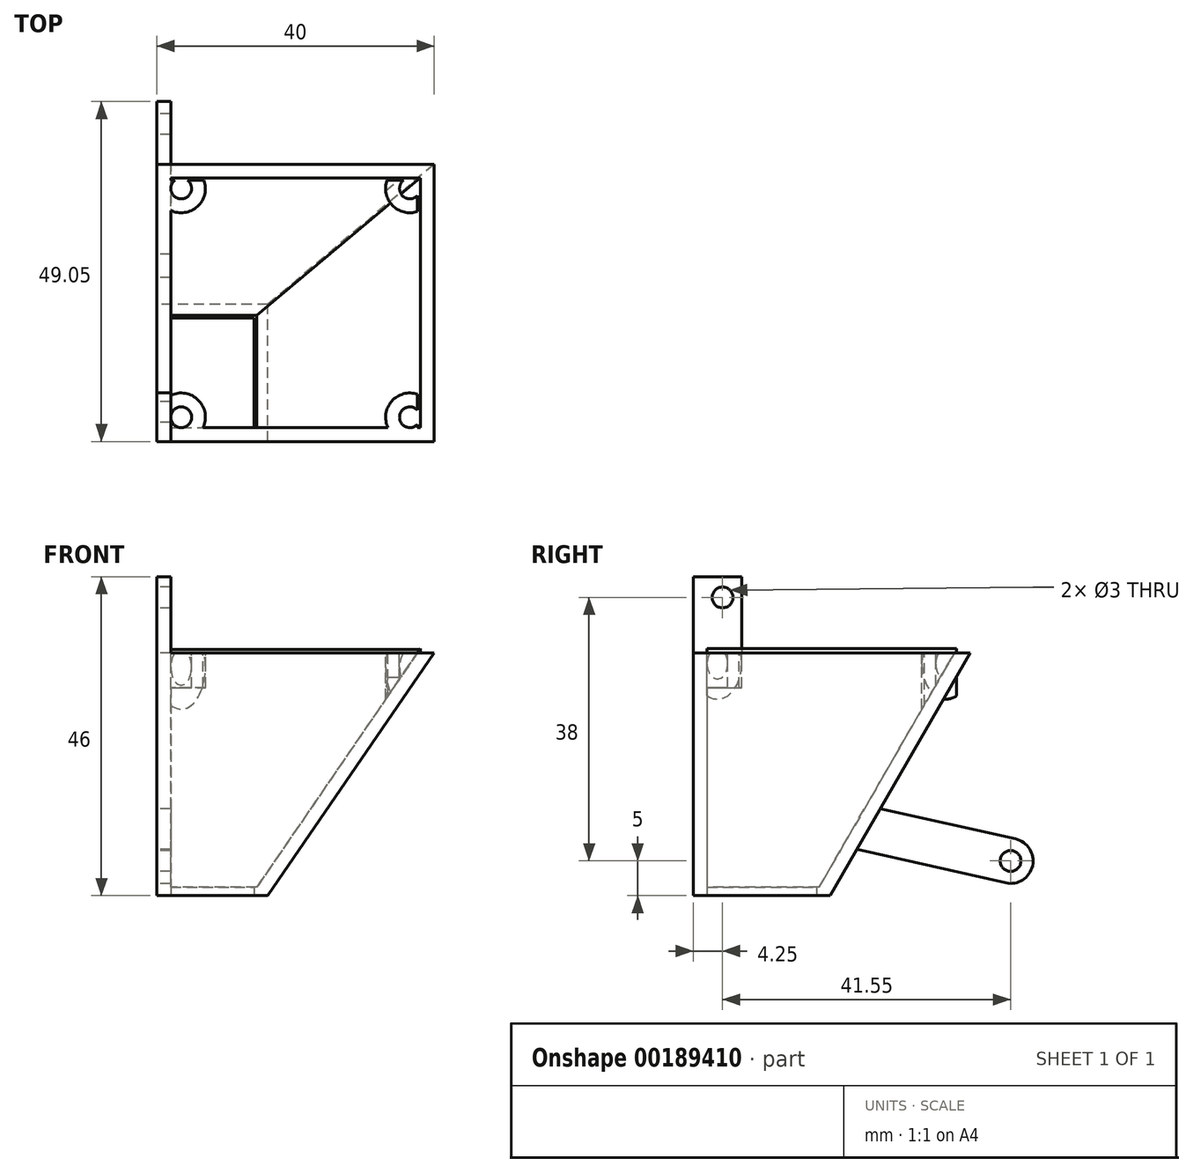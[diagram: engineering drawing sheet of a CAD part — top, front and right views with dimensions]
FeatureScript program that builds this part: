
annotation { "Feature Type Name" : "Feature", "Feature Type Description" : "" }
export const myFeature = defineFeature(function(context is Context, id is Id, definition is map)
    precondition{}
    {
        {
            var Q0;
            Q0=qCreatedBy(makeId("Top.planeOp"),FACE);
            var sketch = newSketch(context, id + "F0", { "sketchPlane" : qUnion([Q0])});
            skLineSegment(sketch, "E0.bottom", {"start": v(0, 0) * mm, "end": v(16, 0) * mm});
            skLineSegment(sketch, "E0.top", {"start": v(0, 19.8) * mm, "end": v(16, 19.8) * mm});
            skLineSegment(sketch, "E0.left", {"start": v(0, 0) * mm, "end": v(0, 19.8) * mm});
            skLineSegment(sketch, "E0.right", {"start": v(16, 0) * mm, "end": v(16, 19.8) * mm});
            skLineSegment(sketch, "E1.0", {"start": v(2, 17.8) * mm, "end": v(14, 17.8) * mm});
            skLineSegment(sketch, "E1.1", {"start": v(2, 2) * mm, "end": v(2, 17.8) * mm});
            skLineSegment(sketch, "E1.2", {"start": v(2, 2) * mm, "end": v(14, 2) * mm});
            skLineSegment(sketch, "E1.3", {"start": v(14, 2) * mm, "end": v(14, 17.8) * mm});
            skSolve(sketch);
        }
        {
            var Q0;
            Q0=qCreatedBy(makeId("Right.planeOp"),FACE);
            var sketch = newSketch(context, id + "F1", { "sketchPlane" : qUnion([Q0])});
            skLineSegment(sketch, "E2", {"start": v(0, 0) * mm, "end": v(0, 35) * mm});
            skLineSegment(sketch, "E3", {"start": v(0, 35) * mm, "end": v(19.8, 35) * mm});
            skLineSegment(sketch, "E4", {"start": v(19.8, 35) * mm, "end": v(40, 35) * mm});
            skLineSegment(sketch, "E5", {"start": v(40, 35) * mm, "end": v(19.8, 0) * mm});
            skLineSegment(sketch, "E6", {"start": v(0, 35) * mm, "end": v(0, 43) * mm, "construction": true});
            skLineSegment(sketch, "E7", {"start": v(0, 43) * mm, "end": v(4.25, 43) * mm, "construction": true});
            skCircle(sketch, "E8", {"center": v(4.25, 43) * mm, "radius": 1.5 * mm});
            skLineSegment(sketch, "E9", {"start": v(0, 35) * mm, "end": v(0, 46) * mm});
            skPoint(sketch, "E9.endSnap0", {"position": v(0, 39) * mm});
            skLineSegment(sketch, "E10", {"start": v(0, 46) * mm, "end": v(7, 46) * mm});
            skLineSegment(sketch, "E11", {"start": v(7, 46) * mm, "end": v(7, 35) * mm});
            skLineSegment(sketch, "E12", {"start": v(19.8, 0) * mm, "end": v(45.8, 0) * mm, "construction": true});
            skLineSegment(sketch, "E13", {"start": v(45.8, 0) * mm, "end": v(45.8, 5) * mm, "construction": true});
            skCircle(sketch, "E14", {"center": v(45.8, 5) * mm, "radius": 1.5 * mm});
            skCircle(sketch, "E15", {"center": v(45.8, 5) * mm, "radius": 3.25 * mm});
            skLineSegment(sketch, "E16", {"start": v(27.04, 12.55) * mm, "end": v(46.51, 8.17) * mm});
            skLineSegment(sketch, "E17", {"start": v(45.09, 1.83) * mm, "end": v(23.64, 6.65) * mm});
            skLineSegment(sketch, "E18", {"start": v(19.8, 0) * mm, "end": v(0, 0) * mm});
            skSolve(sketch);
        }
        {
            var Q0;
            Q0=qCreatedBy(makeId("Front.planeOp"),FACE);
            var sketch = newSketch(context, id + "F2", { "sketchPlane" : qUnion([Q0])});
            skLineSegment(sketch, "E19", {"start": v(40, 35) * mm, "end": v(16, 0) * mm});
            skLineSegment(sketch, "E20", {"start": v(40, 35) * mm, "end": v(0, 35) * mm});
            skLineSegment(sketch, "E21", {"start": v(0, 35) * mm, "end": v(0, 0) * mm});
            skLineSegment(sketch, "E22", {"start": v(0, 0) * mm, "end": v(16, 0) * mm});
            skSolve(sketch);
        }
        {
            var Q0;
            Q0=sQuery(id+"F2.wireOp",EDGE,"E19");
            var Q1;
            Q1=sQuery(id+"F0.wireOp",EDGE,"E0.right");
            cPlane(context, id + "F3", {"entities" : qUnion([Q0, Q1]), "cplaneType" : CPlaneType.LINE_ANGLE, "offset" : 25 * mm, "angle" : 0 * degree, "width" : 150 * mm, "height" : 150 * mm});
        }
        {
            var Q0;
            Q0=qCreatedBy(id+"F3.planeOp",FACE);
            var sketch = newSketch(context, id + "F4", { "sketchPlane" : qUnion([Q0])});
            skLineSegment(sketch, "E23", {"start": v(0, 51.49) * mm, "end": v(40, 51.49) * mm});
            skLineSegment(sketch, "E24", {"start": v(40, 51.49) * mm, "end": v(19.8, 9.05) * mm});
            skLineSegment(sketch, "E25", {"start": v(0, 51.49) * mm, "end": v(0, 9.05) * mm});
            skLineSegment(sketch, "E26", {"start": v(0, 9.05) * mm, "end": v(19.8, 9.05) * mm});
            skSolve(sketch);
        }
        {
            var Q0;
            Q0=sQuery(id+"F4.wireOp",EDGE,"E24");
            cPoint(context, id + "F5", {"entities" : qUnion([Q0]), "parameter" : 0.5});
        }
        {
            var Q0;
            Q0=sQuery(id+"F0.wireOp",EDGE,"E0.top");
            cPoint(context, id + "F6", {"entities" : qUnion([Q0]), "parameter" : 0.5});
        }
        {
            var Q0;
            Q0=sQuery(id+"F1.wireOp",EDGE,"E5");
            cPoint(context, id + "F7", {"entities" : qUnion([Q0]), "parameter" : 0.5});
        }
        {
            var Q0;
            Q0 = qCreatedBy(id + "F5" ,VERTEX);
            var Q1;
            Q1 = qCreatedBy(id + "F6" ,VERTEX);
            var Q2;
            Q2 = qCreatedBy(id + "F7" ,VERTEX);
            cPlane(context, id + "F8", {"entities" : qUnion([Q0, Q1, Q2]), "cplaneType" : CPlaneType.THREE_POINT, "offset" : 25 * mm, "width" : 150 * mm, "height" : 150 * mm});
        }
        {
            var Q0;
            Q0=qCreatedBy(id+"F8.planeOp",FACE);
            var sketch = newSketch(context, id + "F9", { "sketchPlane" : qUnion([Q0])});
            skLineSegment(sketch, "E27", {"start": v(40, 50.3) * mm, "end": v(0, 50.3) * mm});
            skLineSegment(sketch, "E28", {"start": v(40, 50.3) * mm, "end": v(16, 9.9) * mm});
            skLineSegment(sketch, "E29", {"start": v(16, 9.9) * mm, "end": v(0, 9.9) * mm});
            skLineSegment(sketch, "E30", {"start": v(0, 9.9) * mm, "end": v(0, 50.3) * mm});
            skSolve(sketch);
        }
        {
            var Q0;
            Q0=sQuery(id+"F4.wireOp",EDGE,"E23");
            cPoint(context, id + "F10", {"entities" : qUnion([Q0]), "parameter" : 0.5});
        }
        {
            var Q0;
            Q0=sQuery(id+"F2.wireOp",EDGE,"E20");
            cPoint(context, id + "F11", {"entities" : qUnion([Q0]), "parameter" : 0.5});
        }
        {
            var Q0;
            Q0=sQuery(id+"F1.wireOp",VERTEX,"E4.start");
            var Q1;
            Q1 = qCreatedBy(id + "F10" ,VERTEX);
            var Q2;
            Q2 = qCreatedBy(id + "F11" ,VERTEX);
            cPlane(context, id + "F12", {"entities" : qUnion([Q0, Q1, Q2]), "cplaneType" : CPlaneType.THREE_POINT, "offset" : 25 * mm, "width" : 150 * mm, "height" : 150 * mm});
        }
        {
            var Q0;
            Q0=qCreatedBy(id+"F12.planeOp",FACE);
            var sketch = newSketch(context, id + "F13", { "sketchPlane" : qUnion([Q0])});
            skLineSegment(sketch, "E31.bottom", {"start": v(0, 0) * mm, "end": v(40, 0) * mm});
            skLineSegment(sketch, "E31.top", {"start": v(0, 40) * mm, "end": v(40, 40) * mm});
            skLineSegment(sketch, "E31.left", {"start": v(0, 0) * mm, "end": v(0, 40) * mm});
            skLineSegment(sketch, "E31.right", {"start": v(40, 0) * mm, "end": v(40, 40) * mm});
            skLineSegment(sketch, "E32.0", {"start": v(2, 3.5) * mm, "end": v(2, 36.5) * mm});
            skLineSegment(sketch, "E32.1", {"start": v(3.5, 2) * mm, "end": v(36.5, 2) * mm});
            skLineSegment(sketch, "E32.2", {"start": v(38, 3.5) * mm, "end": v(38, 36.5) * mm});
            skLineSegment(sketch, "E32.3", {"start": v(3.5, 38) * mm, "end": v(36.5, 38) * mm});
            skCircle(sketch, "E33", {"center": v(3.5, 36.5) * mm, "radius": 1.5 * mm});
            skCircle(sketch, "E34", {"center": v(3.5, 3.5) * mm, "radius": 1.5 * mm});
            skCircle(sketch, "E35", {"center": v(36.5, 3.5) * mm, "radius": 1.5 * mm});
            skCircle(sketch, "E36", {"center": v(36.5, 36.5) * mm, "radius": 1.5 * mm});
            skArc(sketch, "E37", {"start": v(6.66, 2) * mm, "mid": v(5.97, 5.97) * mm, "end": v(2, 6.66) * mm});
            skArc(sketch, "E38", {"start": v(38, 6.66) * mm, "mid": v(34.03, 5.97) * mm, "end": v(33.34, 2) * mm});
            skArc(sketch, "E39", {"start": v(33.34, 38) * mm, "mid": v(34.03, 34.03) * mm, "end": v(38, 33.34) * mm});
            skArc(sketch, "E40", {"start": v(2, 33.34) * mm, "mid": v(5.97, 34.03) * mm, "end": v(6.66, 38) * mm});
            skLineSegment(sketch, "E41", {"start": v(2, 3.5) * mm, "end": v(2, 2) * mm});
            skLineSegment(sketch, "E42", {"start": v(2, 2) * mm, "end": v(3.5, 2) * mm});
            skLineSegment(sketch, "E43", {"start": v(2, 36.5) * mm, "end": v(2, 38) * mm});
            skLineSegment(sketch, "E44", {"start": v(2, 38) * mm, "end": v(3.5, 38) * mm});
            skLineSegment(sketch, "E45", {"start": v(36.5, 38) * mm, "end": v(38, 38) * mm});
            skLineSegment(sketch, "E46", {"start": v(38, 38) * mm, "end": v(38, 36.5) * mm});
            skLineSegment(sketch, "E47", {"start": v(36.5, 2) * mm, "end": v(38, 2) * mm});
            skLineSegment(sketch, "E48", {"start": v(38, 2) * mm, "end": v(38, 3.5) * mm});
            skSolve(sketch);
        }
        {
            var Q0;
            Q0=sQuery(id+"F0.wireOp",EDGE,"E1.1");
            var Q1;
            Q1=sQuery(id+"F13.wireOp",EDGE,"E32.0");
            cPlane(context, id + "F14", {"entities" : qUnion([Q0, Q1]), "cplaneType" : CPlaneType.LINE_ANGLE, "offset" : 25 * mm, "angle" : 0 * degree, "width" : 150 * mm, "height" : 150 * mm});
        }
        {
            var Q0;
            Q0=qCreatedBy(id+"F14.planeOp",FACE);
            var sketch = newSketch(context, id + "F15", { "sketchPlane" : qUnion([Q0])});
            skLineSegment(sketch, "E49", {"start": v(2, 0) * mm, "end": v(2, 35) * mm});
            skLineSegment(sketch, "E50", {"start": v(17.8, 0) * mm, "end": v(38, 35) * mm});
            skLineSegment(sketch, "E51", {"start": v(38, 35) * mm, "end": v(2, 35) * mm});
            skLineSegment(sketch, "E52", {"start": v(17.8, 0) * mm, "end": v(2, 0) * mm});
            skSolve(sketch);
        }
        {
            var Q0;
            Q0=sQuery(id+"F0.wireOp",EDGE,"E1.3");
            var Q1;
            Q1=sQuery(id+"F13.wireOp",EDGE,"E32.2");
            cPlane(context, id + "F16", {"entities" : qUnion([Q0, Q1]), "cplaneType" : CPlaneType.LINE_ANGLE, "offset" : 25 * mm, "angle" : 0 * degree, "width" : 150 * mm, "height" : 150 * mm});
        }
        {
            var Q0;
            Q0=qCreatedBy(id+"F16.planeOp",FACE);
            var sketch = newSketch(context, id + "F17", { "sketchPlane" : qUnion([Q0])});
            skLineSegment(sketch, "E53", {"start": v(17.8, 7.92) * mm, "end": v(38, 50.36) * mm});
            skLineSegment(sketch, "E54", {"start": v(2, 7.92) * mm, "end": v(2, 50.36) * mm});
            skLineSegment(sketch, "E55", {"start": v(2, 50.36) * mm, "end": v(38, 50.36) * mm});
            skLineSegment(sketch, "E56", {"start": v(2, 7.92) * mm, "end": v(17.8, 7.92) * mm});
            skSolve(sketch);
        }
        {
            var Q0;
            Q0=sQuery(id+"F13.wireOp",EDGE,"E32.3");
            var Q1;
            Q1=sQuery(id+"F0.wireOp",EDGE,"E1.0");
            cPlane(context, id + "F18", {"entities" : qUnion([Q0, Q1]), "cplaneType" : CPlaneType.LINE_ANGLE, "offset" : 25 * mm, "angle" : 0 * degree, "width" : 150 * mm, "height" : 150 * mm});
        }
        {
            var Q0;
            Q0=makeQuery(id+"F4.imprint","IMPRINT",FACE,{"disambiguationData":[TD([[makeQuery(id+"F4.imprint","IMPRINT",EDGE,{"derivedFrom":sQuery(id+"F4.wireOp",EDGE,"E23")}),-1.0]])]});
            extrude(context, id + "F19", {"entities" : qUnion([Q0]), "oppositeDirection" : true, "depth" : 2 * mm});
        }
        {
            var Q0;
            Q0=makeQuery(id+"F9.imprint","IMPRINT",FACE,{"disambiguationData":[TD([[makeQuery(id+"F9.imprint","IMPRINT",EDGE,{"derivedFrom":sQuery(id+"F9.wireOp",EDGE,"E27")}),1.0]])]});
            extrude(context, id + "F20", {"entities" : qUnion([Q0]), "operationType" : NewBodyOperationType.ADD, "depth" : 2 * mm});
        }
        {
            var Q0;
            {var subQ2=sQuery(id+"F1.wireOp",EDGE,"E2");Q0=makeQuery(id+"F1.imprint","IMPRINT",FACE,{"disambiguationData":[TD([[makeQuery(id+"F1.imprint","IMPRINT",EDGE,{"derivedFrom":subQ2}),-1.0]])]});}
            extrude(context, id + "F21", {"entities" : qUnion([Q0]), "operationType" : NewBodyOperationType.ADD, "depth" : 2 * mm});
        }
        {
            var Q0;
            Q0=makeQuery(id+"F2.imprint","IMPRINT",FACE,{"disambiguationData":[TD([[makeQuery(id+"F2.imprint","IMPRINT",EDGE,{"derivedFrom":sQuery(id+"F2.wireOp",EDGE,"E19")}),-1.0]])]});
            extrude(context, id + "F22", {"entities" : qUnion([Q0]), "operationType" : NewBodyOperationType.ADD, "oppositeDirection" : true, "depth" : 2 * mm});
        }
        {
            var Q0;
            Q0=makeQuery(id+"F13.imprint","IMPRINT",FACE,{"disambiguationData":[TD([[makeQuery(id+"F13.imprint","IMPRINT",EDGE,{"derivedFrom":sQuery(id+"F13.wireOp",EDGE,"E31.bottom")}),1.0]])]});
            extrude(context, id + "F23", {"entities" : qUnion([Q0]), "operationType" : NewBodyOperationType.REMOVE, "depth" : 2 * mm});
        }
        {
            var Q0;
            Q0=makeQuery(id+"F0.imprint","IMPRINT",FACE,{"disambiguationData":[TD([[makeQuery(id+"F0.imprint","IMPRINT",EDGE,{"derivedFrom":sQuery(id+"F0.wireOp",EDGE,"E0.bottom")}),1.0]])]});
            extrude(context, id + "F24", {"entities" : qUnion([Q0]), "operationType" : NewBodyOperationType.ADD, "depth" : 1.2 * mm});
        }
        {
            var Q0;
            Q0=makeQuery(id+"F1.imprint","IMPRINT",FACE,{"disambiguationData":[TD([[makeQuery(id+"F1.imprint","IMPRINT",EDGE,{"derivedFrom":sQuery(id+"F1.wireOp",EDGE,"E8")}),-1.0]])]});
            var Q1;
            {var subQ0=sQuery(id+"F1.wireOp",EDGE,"E16");Q1=makeQuery(id+"F1.imprint","IMPRINT",FACE,{"disambiguationData":[TD([[makeQuery(id+"F1.imprint","IMPRINT",EDGE,{"derivedFrom":subQ0}),-1.0]])]});}
            var Q2;
            Q2=makeQuery(id+"F1.imprint","IMPRINT",FACE,{"disambiguationData":[TD([[makeQuery(id+"F1.imprint","IMPRINT",EDGE,{"derivedFrom":sQuery(id+"F1.wireOp",EDGE,"E14")}),-1.0]])]});
            extrude(context, id + "F25", {"entities" : qUnion([Q0, Q1, Q2]), "operationType" : NewBodyOperationType.ADD, "depth" : 2 * mm});
        }
        {
            var Q0;
            {var subQ3=sQuery(id+"F13.wireOp",EDGE,"E38");Q0=makeQuery(id+"F13.imprint","IMPRINT",FACE,{"disambiguationData":[TD([[makeQuery(id+"F13.imprint","IMPRINT",EDGE,{"derivedFrom":subQ3}),1.0]])]});}
            var Q1;
            {var subQ0=sQuery(id+"F13.wireOp",EDGE,"E47");Q1=makeQuery(id+"F13.imprint","IMPRINT",FACE,{"disambiguationData":[TD([[makeQuery(id+"F13.imprint","IMPRINT",EDGE,{"derivedFrom":subQ0}),1.0]])]});}
            var Q2;
            Q2=makeQuery(id+"F19.opExtrude","CAP_FACE",FACE,{"disambiguationData":[OSD([sQuery(id+"F4.wireOp",EDGE,"E23"),sQuery(id+"F4.wireOp",EDGE,"E24"),sQuery(id+"F4.wireOp",EDGE,"E25"),sQuery(id+"F4.wireOp",EDGE,"E26")])],"isStart":false});
            extrude(context, id + "F26", {"entities" : qUnion([Q0, Q1]), "operationType" : NewBodyOperationType.ADD, "endBound" : BoundingType.UP_TO_SURFACE, "oppositeDirection" : true, "endBoundEntityFace" : qUnion([Q2]), "depth" : 25 * mm});
        }
        {
            var Q0;
            {var subQ3=sQuery(id+"F13.wireOp",EDGE,"E37");Q0=makeQuery(id+"F13.imprint","IMPRINT",FACE,{"disambiguationData":[TD([[makeQuery(id+"F13.imprint","IMPRINT",EDGE,{"derivedFrom":subQ3}),1.0]])]});}
            var Q1;
            {var subQ0=sQuery(id+"F13.wireOp",EDGE,"E41");Q1=makeQuery(id+"F13.imprint","IMPRINT",FACE,{"disambiguationData":[TD([[makeQuery(id+"F13.imprint","IMPRINT",EDGE,{"derivedFrom":subQ0}),1.0]])]});}
            extrude(context, id + "F27", {"entities" : qUnion([Q0, Q1]), "operationType" : NewBodyOperationType.ADD, "oppositeDirection" : true, "depth" : 5 * mm});
        }
        {
            var Q0;
            {var subQ3=sQuery(id+"F13.wireOp",EDGE,"E40");Q0=makeQuery(id+"F13.imprint","IMPRINT",FACE,{"disambiguationData":[TD([[makeQuery(id+"F13.imprint","IMPRINT",EDGE,{"derivedFrom":subQ3}),1.0]])]});}
            var Q1;
            {var subQ0=sQuery(id+"F13.wireOp",EDGE,"E43");Q1=makeQuery(id+"F13.imprint","IMPRINT",FACE,{"disambiguationData":[TD([[makeQuery(id+"F13.imprint","IMPRINT",EDGE,{"derivedFrom":subQ0}),-1.0]])]});}
            var Q2;
            {var subQ0=sQuery(id+"F9.wireOp",EDGE,"E29");var subQ1=sQuery(id+"F9.wireOp",EDGE,"E27");var subQ2=sQuery(id+"F4.wireOp",EDGE,"E26");var subQ3=sQuery(id+"F9.wireOp",EDGE,"E30");Q2=makeQuery(id+"F20.boolean.opBoolean","SPLIT",FACE,{"disambiguationData":[TD([makeQuery(id+"F19.opExtrude","SWEPT_FACE",FACE,{"disambiguationData":[OSD([subQ2])]})])],"derivedFrom":makeQuery(id+"F20.opExtrude","CAP_FACE",FACE,{"disambiguationData":[OSD([subQ1,sQuery(id+"F9.wireOp",EDGE,"E28"),subQ0,subQ3])],"isStart":false})});}
            extrude(context, id + "F28", {"entities" : qUnion([Q0, Q1]), "operationType" : NewBodyOperationType.ADD, "endBound" : BoundingType.UP_TO_SURFACE, "oppositeDirection" : true, "endBoundEntityFace" : qUnion([Q2]), "depth" : 25 * mm});
        }
        {
            var Q0;
            {var subQ3=sQuery(id+"F13.wireOp",EDGE,"E39");Q0=makeQuery(id+"F13.imprint","IMPRINT",FACE,{"disambiguationData":[TD([[makeQuery(id+"F13.imprint","IMPRINT",EDGE,{"derivedFrom":subQ3}),1.0]])]});}
            var Q1;
            Q1=makeQuery(id+"F19.opExtrude","CAP_FACE",FACE,{"disambiguationData":[OSD([sQuery(id+"F4.wireOp",EDGE,"E23"),sQuery(id+"F4.wireOp",EDGE,"E24"),sQuery(id+"F4.wireOp",EDGE,"E25"),sQuery(id+"F4.wireOp",EDGE,"E26")])],"isStart":false});
            extrude(context, id + "F29", {"entities" : qUnion([Q0]), "operationType" : NewBodyOperationType.ADD, "endBound" : BoundingType.UP_TO_SURFACE, "oppositeDirection" : true, "endBoundEntityFace" : qUnion([Q1]), "depth" : 25 * mm});
        }
    });
